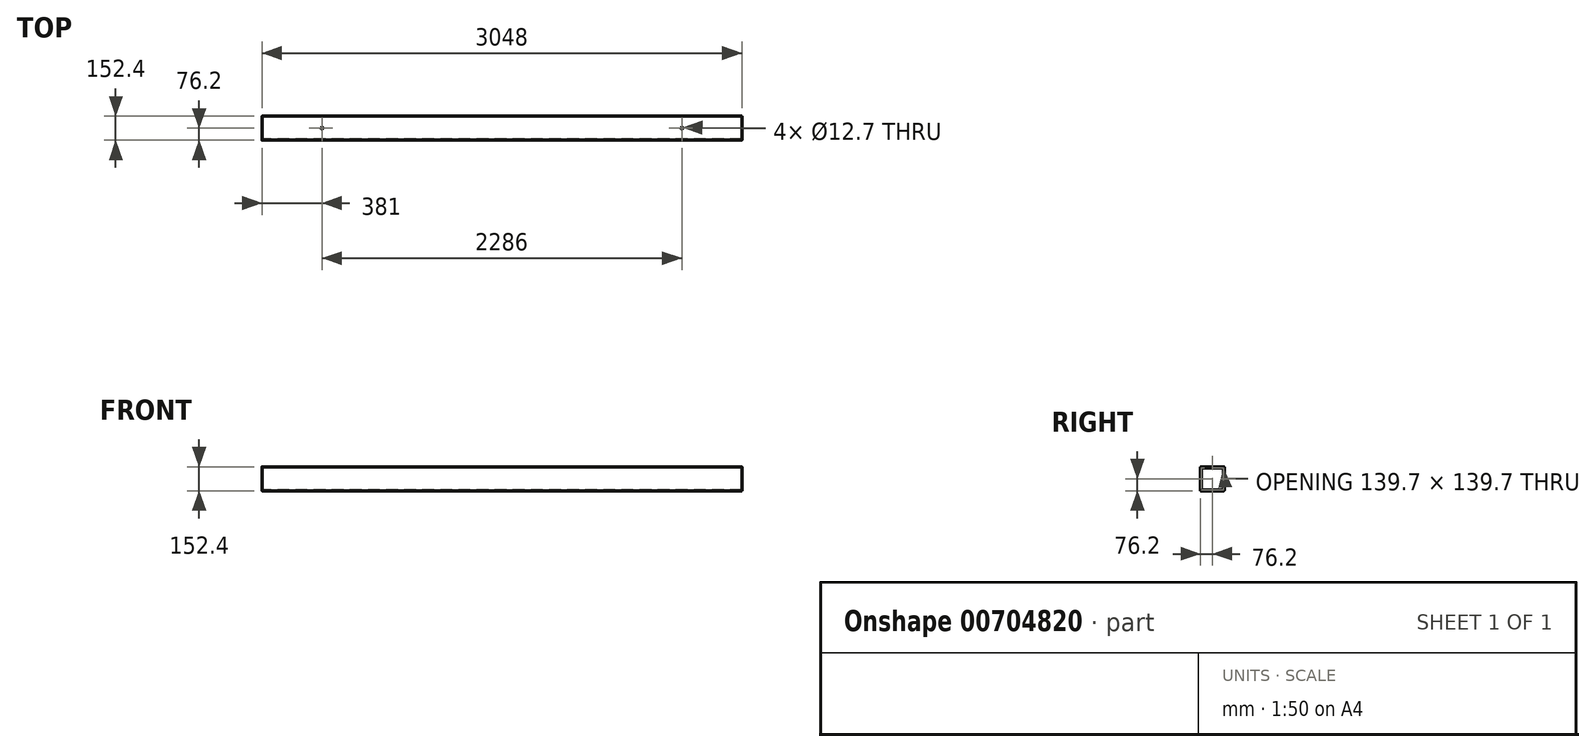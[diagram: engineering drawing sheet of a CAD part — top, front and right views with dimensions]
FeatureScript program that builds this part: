
annotation { "Feature Type Name" : "Feature", "Feature Type Description" : "" }
export const myFeature = defineFeature(function(context is Context, id is Id, definition is map)
    precondition{}
    {
        {
            var Q0;
            Q0=qCreatedBy(makeId("Right.planeOp"),FACE);
            var sketch = newSketch(context, id + "F0", { "sketchPlane" : qUnion([Q0])});
            skLineSegment(sketch, "E0.bottom", {"start": v(-73.03, 76.2) * mm, "end": v(73.03, 76.2) * mm});
            skLineSegment(sketch, "E0.top", {"start": v(-73.03, -76.2) * mm, "end": v(73.02, -76.2) * mm});
            skLineSegment(sketch, "E0.left", {"start": v(-76.2, 73.02) * mm, "end": v(-76.2, -73.03) * mm});
            skLineSegment(sketch, "E0.right", {"start": v(76.2, 73.02) * mm, "end": v(76.2, -73.03) * mm});
            skPoint(sketch, "E0.middle", {"position": v(0, 0) * mm});
            skLineSegment(sketch, "E1.0", {"start": v(-69.85, 66.68) * mm, "end": v(-69.85, -66.67) * mm});
            skLineSegment(sketch, "E2.3", {"start": v(-66.68, -69.85) * mm, "end": v(66.68, -69.85) * mm});
            skLineSegment(sketch, "E3.0", {"start": v(69.85, 66.68) * mm, "end": v(69.85, -66.67) * mm});
            skLineSegment(sketch, "E3.1", {"start": v(-66.68, 69.85) * mm, "end": v(66.68, 69.85) * mm});
            skPoint(sketch, "E4.visualSharp", {"position": v(-76.2, 76.2) * mm});
            skArc(sketch, "E4.filletArc", {"start": v(-73.03, 76.2) * mm, "mid": v(-75.27, 75.27) * mm, "end": v(-76.2, 73.02) * mm});
            skPoint(sketch, "E5.visualSharp", {"position": v(76.2, 76.2) * mm});
            skArc(sketch, "E5.filletArc", {"start": v(76.2, 73.02) * mm, "mid": v(75.27, 75.27) * mm, "end": v(73.03, 76.2) * mm});
            skPoint(sketch, "E6.visualSharp", {"position": v(76.2, -76.2) * mm});
            skArc(sketch, "E6.filletArc", {"start": v(73.02, -76.2) * mm, "mid": v(75.27, -75.27) * mm, "end": v(76.2, -73.03) * mm});
            skPoint(sketch, "E7.visualSharp", {"position": v(-76.2, -76.2) * mm});
            skArc(sketch, "E7.filletArc", {"start": v(-76.2, -73.03) * mm, "mid": v(-75.27, -75.27) * mm, "end": v(-73.03, -76.2) * mm});
            skPoint(sketch, "E8.visualSharp", {"position": v(-69.85, -69.85) * mm});
            skArc(sketch, "E8.filletArc", {"start": v(-69.85, -66.67) * mm, "mid": v(-68.92, -68.92) * mm, "end": v(-66.68, -69.85) * mm});
            skPoint(sketch, "E9.visualSharp", {"position": v(-69.85, 69.85) * mm});
            skArc(sketch, "E9.filletArc", {"start": v(-66.68, 69.85) * mm, "mid": v(-68.92, 68.92) * mm, "end": v(-69.85, 66.68) * mm});
            skPoint(sketch, "E10.visualSharp", {"position": v(69.85, 69.85) * mm});
            skArc(sketch, "E10.filletArc", {"start": v(69.85, 66.68) * mm, "mid": v(68.92, 68.92) * mm, "end": v(66.68, 69.85) * mm});
            skPoint(sketch, "E11.visualSharp", {"position": v(69.85, -69.85) * mm});
            skArc(sketch, "E11.filletArc", {"start": v(66.68, -69.85) * mm, "mid": v(68.92, -68.92) * mm, "end": v(69.85, -66.67) * mm});
            skSolve(sketch);
        }
        {
            var Q0;
            Q0=makeQuery(id+"F0.imprint","IMPRINT",FACE,{"disambiguationData":[TD([[makeQuery(id+"F0.imprint","IMPRINT",EDGE,{"derivedFrom":sQuery(id+"F0.wireOp",EDGE,"E0.bottom")}),-1.0]])]});
            extrude(context, id + "F1", {"entities" : qUnion([Q0]), "flatOperationType" : FlatOperationType.REMOVE, "depth" : 3048 * mm, "hasSecondDirection" : true, "secondDirectionOppositeDirection" : true, "secondDirectionDepth" : 0 * mm, "offsetDistance" : 25.4 * mm, "domain" : OperationDomain.MODEL});
        }
        {
            var Q0;
            Q0=makeQuery(id+"F1.opExtrude","SWEPT_FACE",FACE,{"disambiguationData":[OSD([sQuery(id+"F0.wireOp",EDGE,"E0.top")])]});
            var sketch = newSketch(context, id + "F2", { "sketchPlane" : qUnion([Q0])});
            skPoint(sketch, "E12", {"position": v(2667, 0) * mm});
            skPoint(sketch, "E12.positionSnap0", {"position": v(3048, 0) * mm});
            skPoint(sketch, "E13", {"position": v(381, 0) * mm});
            skPoint(sketch, "E13.positionSnap0", {"position": v(0, 0) * mm});
            skCircle(sketch, "E14", {"center": v(381, 0) * mm, "radius": 6.35 * mm});
            skCircle(sketch, "E15", {"center": v(2667, 0) * mm, "radius": 6.35 * mm});
            skSolve(sketch);
        }
        {
            var Q0;
            Q0=makeQuery(id+"F2.imprint","IMPRINT",FACE,{"disambiguationData":[TD([[makeQuery(id+"F2.imprint","IMPRINT",EDGE,{"derivedFrom":sQuery(id+"F2.wireOp",EDGE,"E14")}),1.0]])]});
            var Q1;
            Q1=makeQuery(id+"F2.imprint","IMPRINT",FACE,{"disambiguationData":[TD([[makeQuery(id+"F2.imprint","IMPRINT",EDGE,{"derivedFrom":sQuery(id+"F2.wireOp",EDGE,"E15")}),1.0]])]});
            extrude(context, id + "F3", {"entities" : qUnion([Q0, Q1]), "operationType" : NewBodyOperationType.REMOVE, "endBound" : BoundingType.THROUGH_ALL, "oppositeDirection" : true, "depth" : 152.4 * mm, "offsetDistance" : 25.4 * mm});
        }
    });
